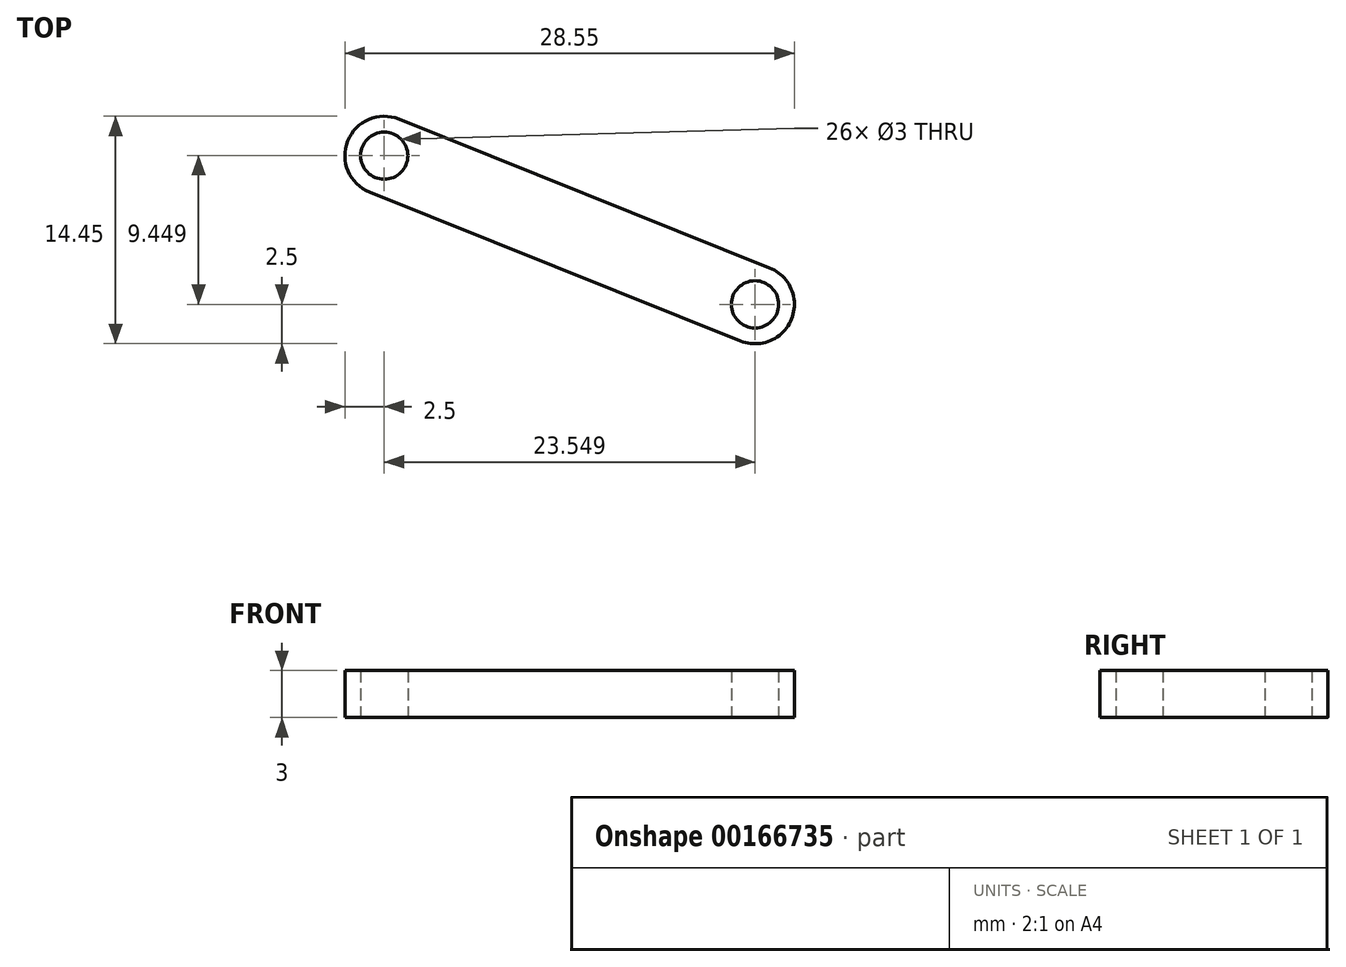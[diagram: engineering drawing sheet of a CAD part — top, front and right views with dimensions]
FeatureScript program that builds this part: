
annotation { "Feature Type Name" : "Feature", "Feature Type Description" : "" }
export const myFeature = defineFeature(function(context is Context, id is Id, definition is map)
    precondition{}
    {
        {
            var Q0;
            Q0=qCreatedBy(makeId("Top.planeOp"),FACE);
            var sketch = newSketch(context, id + "F0", { "sketchPlane" : qUnion([Q0])});
            skLineSegment(sketch, "E0", {"start": v(-9.02, 16.8) * mm, "end": v(14.53, 7.35) * mm});
            skLineSegment(sketch, "E1", {"start": v(14.53, 7.35) * mm, "end": v(12.67, 2.7) * mm});
            skPoint(sketch, "E2", {"position": v(13.6, 5.03) * mm});
            skLineSegment(sketch, "E3", {"start": v(12.67, 2.7) * mm, "end": v(-10.88, 12.16) * mm});
            skLineSegment(sketch, "E4", {"start": v(-10.88, 12.16) * mm, "end": v(-9.02, 16.8) * mm});
            skPoint(sketch, "E5", {"position": v(-9.95, 14.48) * mm});
            skCircle(sketch, "E6", {"center": v(-9.95, 14.48) * mm, "radius": 2.5 * mm});
            skCircle(sketch, "E7", {"center": v(13.6, 5.03) * mm, "radius": 2.5 * mm});
            skCircle(sketch, "E8", {"center": v(-9.95, 14.48) * mm, "radius": 1.5 * mm});
            skCircle(sketch, "E9", {"center": v(13.6, 5.03) * mm, "radius": 1.5 * mm});
            skSolve(sketch);
        }
        {
            var Q0;
            Q0 = qSketchRegion(id + "F0", true);
            extrude(context, id + "F1", {"entities" : qUnion([Q0]), "depth" : 3 * mm});
        }
    });
